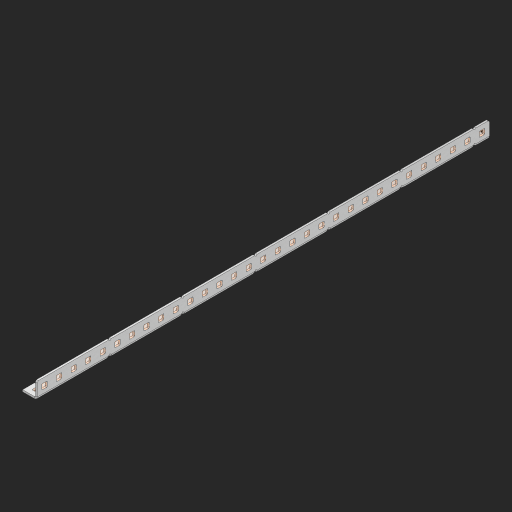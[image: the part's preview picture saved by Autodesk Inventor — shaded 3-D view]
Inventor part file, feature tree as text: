
AUTODESK INVENTOR PART (.ipt)
format: ipt  version: 2023 (Build 270158000, 158)  size: 1,283,584 bytes
history: native  units: in
note: dims shown in document units (in); Inventor stores cm internally (conversion verified against a paired STEP export)
features: other x241, extrude x91, sheet_metal_op x11, sketch x10, pattern_linear x2, mirror x1, chamfer x1
ambient origin geometry x8: Origin, YZ Plane, XZ Plane, XY Plane, X Axis, Y Axis, Z Axis, Center Point
bodies: Solid1 (feature_tree), Body (feature_tree)
feature tree (357):
  other  "Alu Half C 1x2x1x31"
  other  "Table"
  other  "Alu C 1x2x1x35"
  other  "Alu C 1x2x1x34"
  other  "Alu C 1x2x1x33"
  other  "Alu C 1x2x1x32"
  other  "Alu C 1x2x1x31"
  other  "Alu C 1x2x1x30"
  other  "Alu C 1x2x1x29"
  other  "Alu C 1x2x1x28"
  other  "Alu C 1x2x1x27"
  other  "Alu C 1x2x1x26"
  other  "Alu C 1x2x1x25"
  other  "Alu C 1x2x1x24"
  other  "Alu C 1x2x1x23"
  other  "Alu C 1x2x1x22"
  other  "Alu C 1x2x1x21"
  other  "Alu C 1x2x1x20"
  other  "Alu C 1x2x1x19"
  other  "Alu C 1x2x1x18"
  other  "Alu C 1x2x1x17"
  other  "Alu C 1x2x1x16"
  other  "Alu C 1x2x1x15"
  other  "Alu C 1x2x1x14"
  other  "Alu C 1x2x1x13"
  other  "Alu C 1x2x1x12"
  other  "Alu C 1x2x1x11"
  other  "Alu C 1x2x1x10"
  other  "Alu C 1x2x1x9"
  other  "Alu C 1x2x1x8"
  other  "Alu C 1x2x1x7"
  other  "Alu C 1x2x1x6"
  other  "Alu C 1x2x1x5"
  other  "Alu C 1x2x1x4"
  other  "Alu C 1x2x1x3"
  other  "Alu C 1x2x1x2"
  other  "Alu C 1x2x1x1"
  other  "Steel C 1x2x1x35"
  other  "Steel C 1x2x1x34"
  other  "Steel C 1x2x1x33"
  other  "Steel C 1x2x1x32"
  other  "Steel C 1x2x1x31"
  other  "Steel C 1x2x1x30"
  other  "Steel C 1x2x1x29"
  other  "Steel C 1x2x1x28"
  other  "Steel C 1x2x1x27"
  other  "Steel C 1x2x1x26"
  other  "Steel C 1x2x1x25"
  other  "Steel C 1x2x1x24"
  other  "Steel C 1x2x1x23"
  other  "Steel C 1x2x1x22"
  other  "Steel C 1x2x1x21"
  other  "Steel C 1x2x1x20"
  other  "Steel C 1x2x1x19"
  other  "Steel C 1x2x1x18"
  other  "Steel C 1x2x1x17"
  other  "Steel C 1x2x1x16"
  other  "Steel C 1x2x1x15"
  other  "Steel C 1x2x1x14"
  other  "Steel C 1x2x1x13"
  other  "Steel C 1x2x1x12"
  other  "Steel C 1x2x1x11"
  other  "Steel C 1x2x1x10"
  other  "Steel C 1x2x1x9"
  other  "Steel C 1x2x1x8"
  other  "Steel C 1x2x1x7"
  other  "Steel C 1x2x1x6"
  other  "Steel C 1x2x1x5"
  other  "Steel C 1x2x1x4"
  other  "Steel C 1x2x1x3"
  other  "Steel C 1x2x1x2"
  other  "Steel C 1x2x1x1"
  other  "Alu Half C 1x2x1x35"
  other  "Alu Half C 1x2x1x34"
  other  "Alu Half C 1x2x1x33"
  other  "Alu Half C 1x2x1x32"
  other  "Alu Half C 1x2x1x30"
  other  "Alu Half C 1x2x1x29"
  other  "Alu Half C 1x2x1x28"
  other  "Alu Half C 1x2x1x27"
  other  "Alu Half C 1x2x1x26"
  other  "Alu Half C 1x2x1x25"
  other  "Alu Half C 1x2x1x24"
  other  "Alu Half C 1x2x1x23"
  other  "Alu Half C 1x2x1x22"
  other  "Alu Half C 1x2x1x21"
  other  "Alu Half C 1x2x1x20"
  other  "Alu Half C 1x2x1x19"
  other  "Alu Half C 1x2x1x18"
  other  "Alu Half C 1x2x1x17"
  other  "Alu Half C 1x2x1x16"
  other  "Alu Half C 1x2x1x15"
  other  "Alu Half C 1x2x1x14"
  other  "Alu Half C 1x2x1x13"
  other  "Alu Half C 1x2x1x12"
  other  "Alu Half C 1x2x1x11"
  other  "Alu Half C 1x2x1x10"
  other  "Alu Half C 1x2x1x9"
  other  "Alu Half C 1x2x1x8"
  other  "Alu Half C 1x2x1x7"
  other  "Alu Half C 1x2x1x6"
  other  "Alu Half C 1x2x1x5"
  other  "Alu Half C 1x2x1x4"
  other  "Alu Half C 1x2x1x3"
  other  "Alu Half C 1x2x1x2"
  other  "Alu Half C 1x2x1x1"
  other  "Steel Half C 1x2x1x35"
  other  "Steel Half C 1x2x1x34"
  other  "Steel Half C 1x2x1x33"
  other  "Steel Half C 1x2x1x32"
  other  "Steel Half C 1x2x1x31"
  other  "Steel Half C 1x2x1x30"
  other  "Steel Half C 1x2x1x29"
  other  "Steel Half C 1x2x1x28"
  other  "Steel Half C 1x2x1x27"
  other  "Steel Half C 1x2x1x26"
  other  "Steel Half C 1x2x1x25"
  other  "Steel Half C 1x2x1x24"
  other  "Steel Half C 1x2x1x23"
  other  "Steel Half C 1x2x1x22"
  other  "Steel Half C 1x2x1x21"
  other  "Steel Half C 1x2x1x20"
  other  "Steel Half C 1x2x1x19"
  other  "Steel Half C 1x2x1x18"
  other  "Steel Half C 1x2x1x17"
  other  "Steel Half C 1x2x1x16"
  other  "Steel Half C 1x2x1x15"
  other  "Steel Half C 1x2x1x14"
  other  "Steel Half C 1x2x1x13"
  other  "Steel Half C 1x2x1x12"
  other  "Steel Half C 1x2x1x11"
  other  "Steel Half C 1x2x1x10"
  other  "Steel Half C 1x2x1x9"
  other  "Steel Half C 1x2x1x8"
  other  "Steel Half C 1x2x1x7"
  other  "Steel Half C 1x2x1x6"
  other  "Steel Half C 1x2x1x5"
  other  "Steel Half C 1x2x1x4"
  other  "Steel Half C 1x2x1x3"
  other  "Steel Half C 1x2x1x2"
  other  "Steel Half C 1x2x1x1"
  sheet_metal_op  "Flanges"
  other  "Flange Pattern Plane"
  other  "Flange Pattern Sketch"
  sheet_metal_op  "Flange Pattern"
  sheet_metal_op  "Body Pattern"
  pattern_linear  "Center Pattern"  Spacing1=0.0625in  [1 undecoded]
  other  "Arc Length"
  mirror  "Notch Mirror"
  pattern_linear  "Notch Pattern"  Spacing1=0.182in  [1 undecoded]
  chamfer  "End Chamfer"
  extrude  "Half Cut"  Depth=0.02in
  sketch  "Sketch1"  dims[d0=1.0in]
  other  "Plate1"
  sketch  "Sketch2"  dims[d1=15.5in]
  other  "Plate2"
  sheet_metal_op  "Bend1"
  sheet_metal_op  "Corner1"
  sketch  "Sketch3"  dims[d2=0.0625in]
  sketch  "Sketch7"  dims[d3=0.0625in]
  other  "Srf1"
  other  "Srf2"
  sketch  "Sketch8"  dims[d4=0.0312in]
  sketch  "Sketch9"  dims[d5=0.125in]
  other  "Srf91"
  sheet_metal_op  "Body Pattern Sketch"
  other  "Srf92"
  sketch  "Sketch13"  dims[d6=0.0625in]
  sketch  "Sketch14"  dims[d7=0.5in d8=90.0deg d9=0.0312in]
  sketch  "Sketch15"  dims[d10=0.25in]
  sketch  "Sketch16"  dims[d11=0.0625in d12=0.0625in d16=0.182in d17=0.02in d18=0.0625in d19=0.0in d20=0.25in d21=0.25in d38=12.2047in d40=0.5in d41=0.3937in d43=1.0in d46=0.172in d47=1.0in d48=0.0in d49=0.182in d50=0.02in d51=0.25in d52=0.25in d53=0.0625in d54=0.0in d55=0.172in d56=1.0in d57=0.0in d58=0.25in d60=12.2047in d62=0.5in d63=0.3937in d65=0.5in d85=0.1473in d86=0.1782in d88=0.04in d89=0.0625in d90=0.0in d91=0.04in d92=0.0491in d95=2.5in d96=0.04in d97=0.25in d98=45.0deg d99=0.25in d100=0.5in d101=0.0in d102=2.497in d106=0.182in d107=0.02in d108=0.5in d109=0.5in d110=0.0625in d111=0.0in d112=0.172in d113=0.5in d114=0.0in d117=0.5in d118=0.5in d119=0.5in]
  other  "Srf786"
  other  "Srf823"
  other  "Srf824"
  other  "Srf825"
  other  "Srf826"
  other  "Srf827"
  other  "Srf828"
  other  "Srf829"
  other  "Srf856"
  other  "Srf857"
  other  "Srf858"
  other  "Srf859"
  other  "Srf860"
  other  "Srf861"
  other  "Srf862"
  other  "Srf889"
  other  "Srf890"
  other  "Srf891"
  other  "Srf892"
  other  "Srf893"
  other  "Srf894"
  other  "Srf895"
  other  "Srf896"
  other  "Srf922"
  other  "Srf923"
  other  "Srf924"
  other  "Srf925"
  other  "Srf926"
  other  "Srf959"
  other  "Srf960"
  other  "Srf961"
  other  "Srf962"
  other  "Srf963"
  other  "Srf996"
  other  "Srf997"
  other  "Srf998"
  other  "Srf999"
  other  "Srf1000"
  other  "Srf1143"
  other  "Srf1144"
  other  "Srf1145"
  other  "Srf1146"
  other  "Srf1147"
  other  "Srf1148"
  other  "Srf1149"
  other  "Srf1150"
  other  "Srf1151"
  other  "Srf1152"
  other  "Srf1153"
  other  "Srf1154"
  other  "Srf1155"
  other  "Srf1156"
  other  "Srf1157"
  other  "Srf1158"
  other  "Srf1159"
  other  "Srf1199"
  other  "Srf1200"
  other  "Srf1201"
  other  "Srf1202"
  other  "Srf1203"
  other  "Srf1204"
  other  "Srf1205"
  other  "Srf1206"
  other  "Srf1207"
  other  "Srf1208"
  other  "Srf1209"
  other  "Srf1210"
  other  "Srf1211"
  other  "Srf1212"
  other  "Srf1213"
  other  "Srf1214"
  other  "Srf1215"
  other  "Srf1255"
  other  "Srf1256"
  other  "Srf1257"
  other  "Srf1258"
  other  "Srf1259"
  other  "Srf1260"
  other  "Srf1261"
  other  "Srf1262"
  other  "Srf1263"
  other  "Srf1264"
  other  "Srf1265"
  other  "Srf1266"
  other  "Srf1267"
  other  "Srf1268"
  other  "Srf1269"
  other  "Srf1270"
  other  "Srf1271"
  sheet_metal_op  "Flange Stamp"
  sheet_metal_op  "Flange Circle"
  sheet_metal_op  "Body Stamp"
  sheet_metal_op  "Body Circle"
  other  "Center Stamp"
  other  "Center Circle"
  sheet_metal_op  "Notch"
  extrude  "ExtrusionSrf2"  Depth=0.0625in
  extrude  "ExtrusionSrf92"  TaperAngle=0.0deg  [1 undecoded]
  extrude  "ExtrusionSrf823"  Depth=0.5in
  extrude  "ExtrusionSrf824"  Depth=0.5in
  extrude  "ExtrusionSrf825"  Depth=0.5in
  extrude  "ExtrusionSrf826"  Depth=0.5in
  extrude  "ExtrusionSrf827"  Depth=1.0in TaperAngle=0.0deg
  extrude  "ExtrusionSrf828"  Depth=0.182in
  extrude  "ExtrusionSrf829"  Depth=0.02in
  extrude  "ExtrusionSrf856"  Depth=0.5in
  extrude  "ExtrusionSrf857"  Depth=0.5in
  extrude  "ExtrusionSrf858"  Depth=0.0625in
  extrude  "ExtrusionSrf859"  TaperAngle=0.0deg  [1 undecoded]
  extrude  "ExtrusionSrf860"  Depth=0.5in
  extrude  "ExtrusionSrf861"  Depth=1.0in TaperAngle=0.0deg
  extrude  "ExtrusionSrf862"  Depth=0.5in
  extrude  "ExtrusionSrf889"  Depth=0.5in
  extrude  "ExtrusionSrf890"  Depth=0.5in
  extrude  "ExtrusionSrf891"  Depth=0.5in
  extrude  "ExtrusionSrf892"  Depth=0.5in
  extrude  "ExtrusionSrf893"  Depth=0.5in
  extrude  "ExtrusionSrf894"  Depth=0.0625in
  extrude  "ExtrusionSrf895"  TaperAngle=0.0deg  [1 undecoded]
  extrude  "ExtrusionSrf896"  Depth=0.5in
  extrude  "ExtrusionSrf922"  Depth=0.5in
  extrude  "ExtrusionSrf923"  Depth=0.5in
  extrude  "ExtrusionSrf924"  Depth=0.5in TaperAngle=45.0deg
  extrude  "ExtrusionSrf925"  Depth=0.5in
  extrude  "ExtrusionSrf926"  Depth=0.5in TaperAngle=0.0deg
  extrude  "ExtrusionSrf959"  Depth=0.5in
  extrude  "ExtrusionSrf960"  Depth=0.182in
  extrude  "ExtrusionSrf961"  Depth=0.02in
  extrude  "ExtrusionSrf962"  Depth=0.5in
  extrude  "ExtrusionSrf963"  Depth=0.5in
  extrude  "ExtrusionSrf996"  Depth=0.0625in
  extrude  "ExtrusionSrf997"  TaperAngle=0.0deg  [1 undecoded]
  extrude  "ExtrusionSrf998"  Depth=0.5in
  extrude  "ExtrusionSrf999"  Depth=0.5in TaperAngle=0.0deg
  extrude  "ExtrusionSrf1000"  Depth=0.5in
  extrude  "ExtrusionSrf1143"  Depth=0.5in
  extrude  "ExtrusionSrf1144"  Depth=0.5in
  extrude  "ExtrusionSrf1145"  [1 undecoded]
  extrude  "ExtrusionSrf1146"  [1 undecoded]
  extrude  "ExtrusionSrf1147"  [1 undecoded]
  extrude  "ExtrusionSrf1148"  [1 undecoded]
  extrude  "ExtrusionSrf1149"  [1 undecoded]
  extrude  "ExtrusionSrf1150"  [1 undecoded]
  extrude  "ExtrusionSrf1151"  [1 undecoded]
  extrude  "ExtrusionSrf1152"  [1 undecoded]
  extrude  "ExtrusionSrf1153"  [1 undecoded]
  extrude  "ExtrusionSrf1154"  [1 undecoded]
  extrude  "ExtrusionSrf1155"  [1 undecoded]
  extrude  "ExtrusionSrf1156"  [1 undecoded]
  extrude  "ExtrusionSrf1157"  [1 undecoded]
  extrude  "ExtrusionSrf1158"  [1 undecoded]
  extrude  "ExtrusionSrf1159"  [1 undecoded]
  extrude  "ExtrusionSrf1199"  [1 undecoded]
  extrude  "ExtrusionSrf1200"  [1 undecoded]
  extrude  "ExtrusionSrf1201"  [1 undecoded]
  extrude  "ExtrusionSrf1202"  [1 undecoded]
  extrude  "ExtrusionSrf1203"  [1 undecoded]
  extrude  "ExtrusionSrf1204"  [1 undecoded]
  extrude  "ExtrusionSrf1205"  [1 undecoded]
  extrude  "ExtrusionSrf1206"  [1 undecoded]
  extrude  "ExtrusionSrf1207"  [1 undecoded]
  extrude  "ExtrusionSrf1208"  [1 undecoded]
  extrude  "ExtrusionSrf1209"  [1 undecoded]
  extrude  "ExtrusionSrf1210"  [1 undecoded]
  extrude  "ExtrusionSrf1211"  [1 undecoded]
  extrude  "ExtrusionSrf1212"  [1 undecoded]
  extrude  "ExtrusionSrf1213"  [1 undecoded]
  extrude  "ExtrusionSrf1214"  [1 undecoded]
  extrude  "ExtrusionSrf1215"  [1 undecoded]
  extrude  "ExtrusionSrf1255"  [1 undecoded]
  extrude  "ExtrusionSrf1256"  [1 undecoded]
  extrude  "ExtrusionSrf1257"  [1 undecoded]
  extrude  "ExtrusionSrf1258"  [1 undecoded]
  extrude  "ExtrusionSrf1259"  [1 undecoded]
  extrude  "ExtrusionSrf1260"  [1 undecoded]
  extrude  "ExtrusionSrf1261"  [1 undecoded]
  extrude  "ExtrusionSrf1262"  [1 undecoded]
  extrude  "ExtrusionSrf1263"  [1 undecoded]
  extrude  "ExtrusionSrf1264"  [1 undecoded]
  extrude  "ExtrusionSrf1265"  [1 undecoded]
  extrude  "ExtrusionSrf1266"  [1 undecoded]
  extrude  "ExtrusionSrf1267"  [1 undecoded]
  extrude  "ExtrusionSrf1268"  [1 undecoded]
  extrude  "ExtrusionSrf1269"  [1 undecoded]
  extrude  "ExtrusionSrf1270"  [1 undecoded]
  extrude  "ExtrusionSrf1271"  [1 undecoded]
note: 55 required parameter values undecoded (feature->parameter linkage not recoverable at this tier; creation-order binding heuristic only, values carry confidence <= 0.55)
